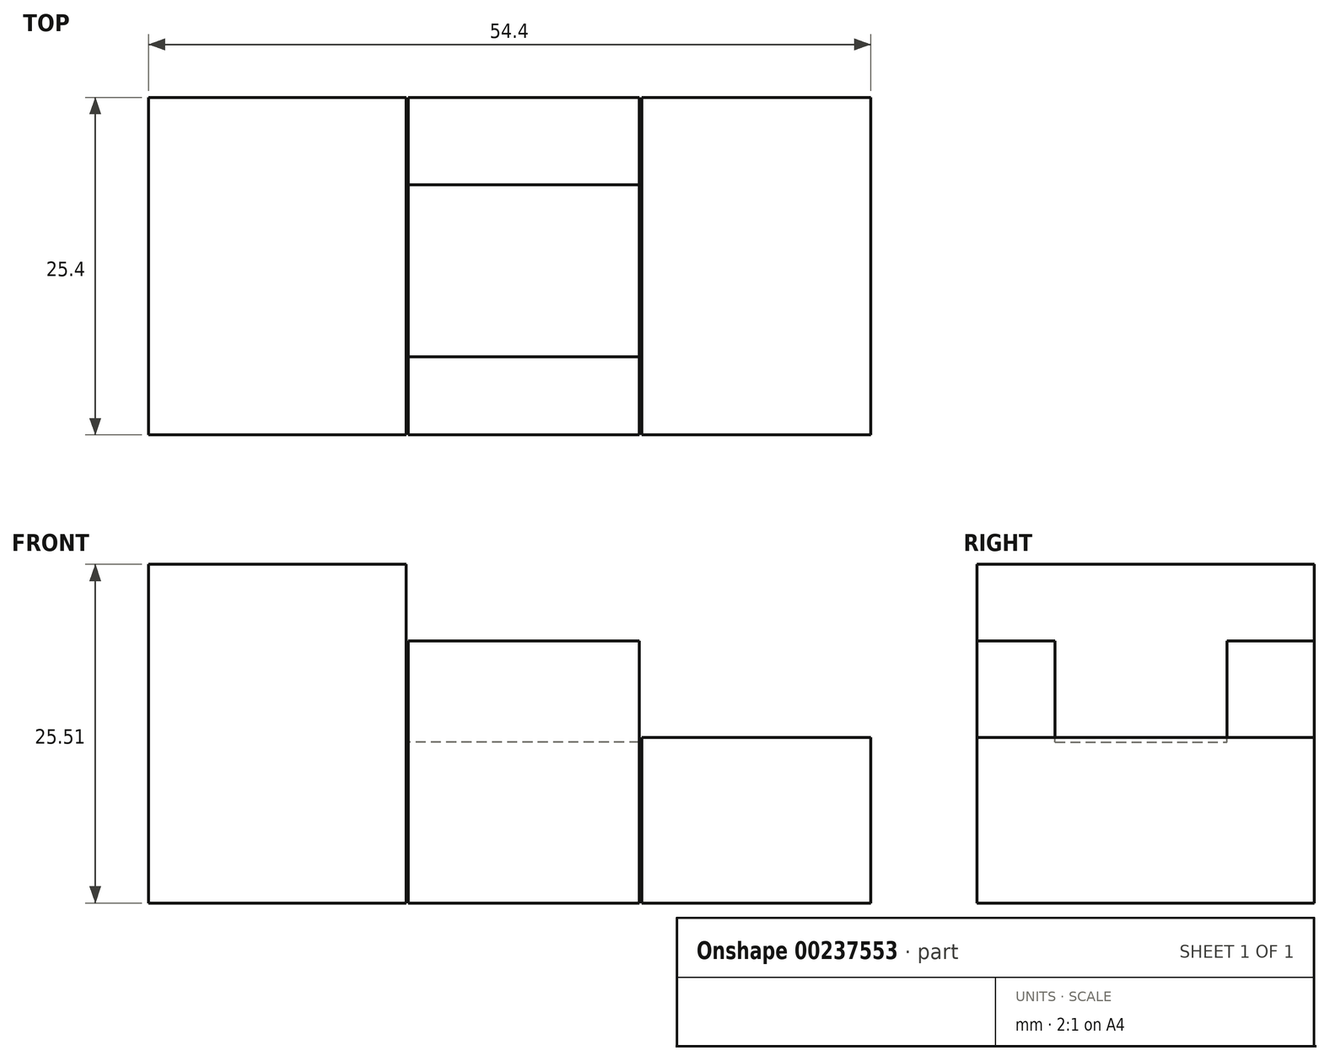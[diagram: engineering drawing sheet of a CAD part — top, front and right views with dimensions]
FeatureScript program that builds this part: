
annotation { "Feature Type Name" : "Feature", "Feature Type Description" : "" }
export const myFeature = defineFeature(function(context is Context, id is Id, definition is map)
    precondition{}
    {
        {
            var Q0;
            Q0=qCreatedBy(makeId("Front.planeOp"),FACE);
            var sketch = newSketch(context, id + "F0", { "sketchPlane" : qUnion([Q0])});
            skLineSegment(sketch, "E0.bottom", {"start": v(-27.54, 0) * mm, "end": v(-46.96, 0) * mm});
            skLineSegment(sketch, "E0.top", {"start": v(-27.54, 25.51) * mm, "end": v(-46.96, 25.51) * mm});
            skLineSegment(sketch, "E0.left", {"start": v(-27.54, 0) * mm, "end": v(-27.54, 25.51) * mm});
            skLineSegment(sketch, "E0.right", {"start": v(-46.96, 0) * mm, "end": v(-46.96, 25.51) * mm});
            skSolve(sketch);
        }
        {
            var Q0;
            Q0=qCreatedBy(makeId("Front.planeOp"),FACE);
            var sketch = newSketch(context, id + "F1", { "sketchPlane" : qUnion([Q0])});
            skLineSegment(sketch, "E1.bottom", {"start": v(-27.4, 19.74) * mm, "end": v(-9.98, 19.74) * mm});
            skLineSegment(sketch, "E1.top", {"start": v(-27.4, 0) * mm, "end": v(-9.98, 0) * mm});
            skLineSegment(sketch, "E1.left", {"start": v(-27.4, 19.74) * mm, "end": v(-27.4, 0) * mm});
            skLineSegment(sketch, "E1.right", {"start": v(-9.98, 19.74) * mm, "end": v(-9.98, 0) * mm});
            skSolve(sketch);
        }
        {
            var Q0;
            Q0=qCreatedBy(makeId("Front.planeOp"),FACE);
            var sketch = newSketch(context, id + "F2", { "sketchPlane" : qUnion([Q0])});
            skLineSegment(sketch, "E2.bottom", {"start": v(-9.81, 12.47) * mm, "end": v(7.44, 12.47) * mm});
            skLineSegment(sketch, "E2.top", {"start": v(-9.81, 0) * mm, "end": v(7.44, 0) * mm});
            skLineSegment(sketch, "E2.left", {"start": v(-9.81, 12.47) * mm, "end": v(-9.81, 0) * mm});
            skLineSegment(sketch, "E2.right", {"start": v(7.44, 12.47) * mm, "end": v(7.44, 0) * mm});
            skSolve(sketch);
        }
        {
            var Q0;
            Q0=makeQuery(id+"F0.imprint","IMPRINT",FACE,{"disambiguationData":[TD([[makeQuery(id+"F0.imprint","IMPRINT",EDGE,{"derivedFrom":sQuery(id+"F0.wireOp",EDGE,"E0.bottom")}),-1.0]])]});
            extrude(context, id + "F3", {"entities" : qUnion([Q0]), "depth" : 25.4 * mm});
        }
        {
            var Q0;
            Q0=makeQuery(id+"F1.imprint","IMPRINT",FACE,{"disambiguationData":[TD([[makeQuery(id+"F1.imprint","IMPRINT",EDGE,{"derivedFrom":sQuery(id+"F1.wireOp",EDGE,"E1.bottom")}),-1.0]])]});
            extrude(context, id + "F4", {"entities" : qUnion([Q0]), "depth" : 25.4 * mm});
        }
        {
            var Q0;
            Q0=makeQuery(id+"F2.imprint","IMPRINT",FACE,{"disambiguationData":[TD([[makeQuery(id+"F2.imprint","IMPRINT",EDGE,{"derivedFrom":sQuery(id+"F2.wireOp",EDGE,"E2.bottom")}),-1.0]])]});
            extrude(context, id + "F5", {"entities" : qUnion([Q0]), "depth" : 25.4 * mm});
        }
        {
            var Q0;
            Q0=makeQuery(id+"F4.opExtrude","SWEPT_FACE",FACE,{"disambiguationData":[OSD([sQuery(id+"F1.wireOp",EDGE,"E1.bottom")])]});
            var sketch = newSketch(context, id + "F6", { "sketchPlane" : qUnion([Q0])});
            skLineSegment(sketch, "E3.bottom", {"start": v(-9.98, -19.51) * mm, "end": v(-27.93, -19.51) * mm});
            skLineSegment(sketch, "E3.top", {"start": v(-9.98, -6.55) * mm, "end": v(-27.93, -6.55) * mm});
            skLineSegment(sketch, "E3.left", {"start": v(-9.98, -19.51) * mm, "end": v(-9.98, -6.55) * mm});
            skLineSegment(sketch, "E3.right", {"start": v(-27.93, -19.51) * mm, "end": v(-27.93, -6.55) * mm});
            skPoint(sketch, "E3.middle", {"position": v(-18.96, -13.03) * mm});
            skSolve(sketch);
        }
        {
            var Q0;
            {var subQ0=sQuery(id+"F6.wireOp",EDGE,"E3.left");Q0=makeQuery(id+"F6.imprint","IMPRINT",FACE,{"disambiguationData":[TD([[makeQuery(id+"F6.imprint","IMPRINT",EDGE,{"derivedFrom":subQ0}),1.0]])]});}
            extrude(context, id + "F7", {"entities" : qUnion([Q0]), "operationType" : NewBodyOperationType.REMOVE, "oppositeDirection" : true, "depth" : 7.62 * mm});
        }
    });
